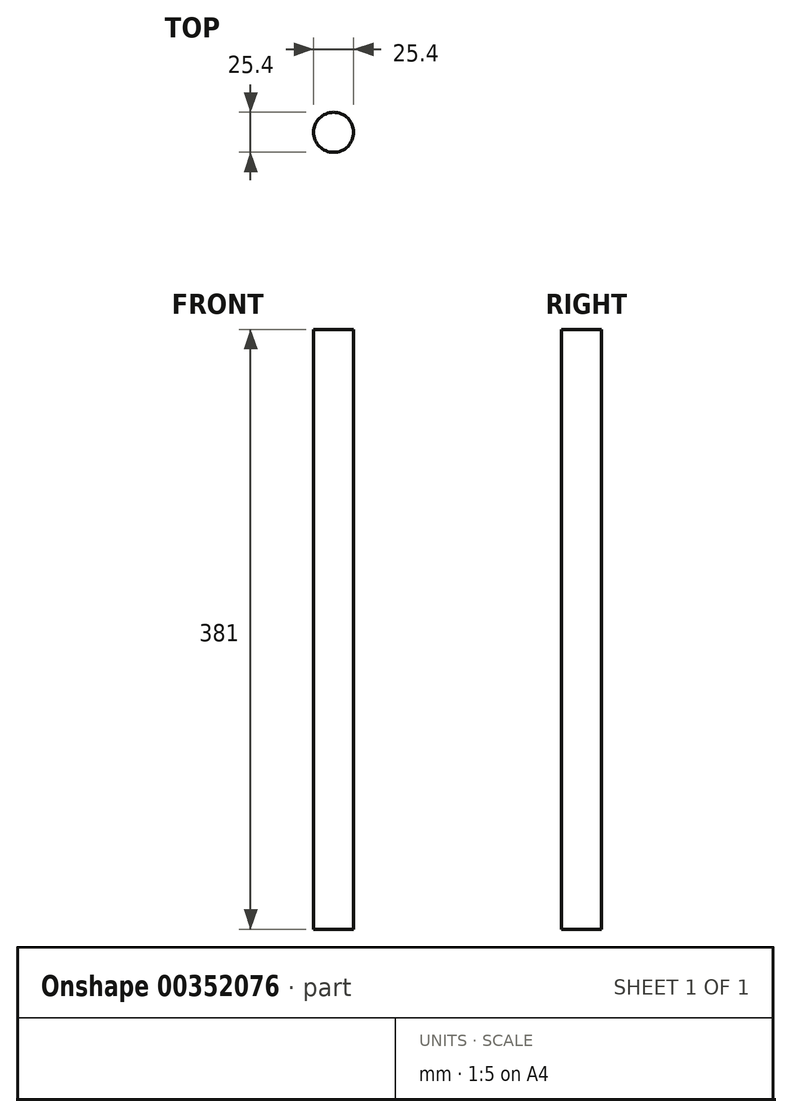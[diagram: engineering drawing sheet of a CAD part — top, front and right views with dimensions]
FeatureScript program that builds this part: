
annotation { "Feature Type Name" : "Feature", "Feature Type Description" : "" }
export const myFeature = defineFeature(function(context is Context, id is Id, definition is map)
    precondition{}
    {
        {
            var Q0;
            Q0=qCreatedBy(makeId("Top.planeOp"),FACE);
            var sketch = newSketch(context, id + "F0", { "sketchPlane" : qUnion([Q0])});
            skCircle(sketch, "E0", {"center": v(0, 0) * mm, "radius": 12.7 * mm});
            skSolve(sketch);
        }
        {
            var Q0;
            Q0=makeQuery(id+"F0.imprint","IMPRINT",FACE,{"disambiguationData":[TD([[makeQuery(id+"F0.imprint","IMPRINT",EDGE,{"derivedFrom":sQuery(id+"F0.wireOp",EDGE,"E0")}),1.0]])]});
            extrude(context, id + "F1", {"entities" : qUnion([Q0]), "depth" : 381 * mm});
        }
    });
